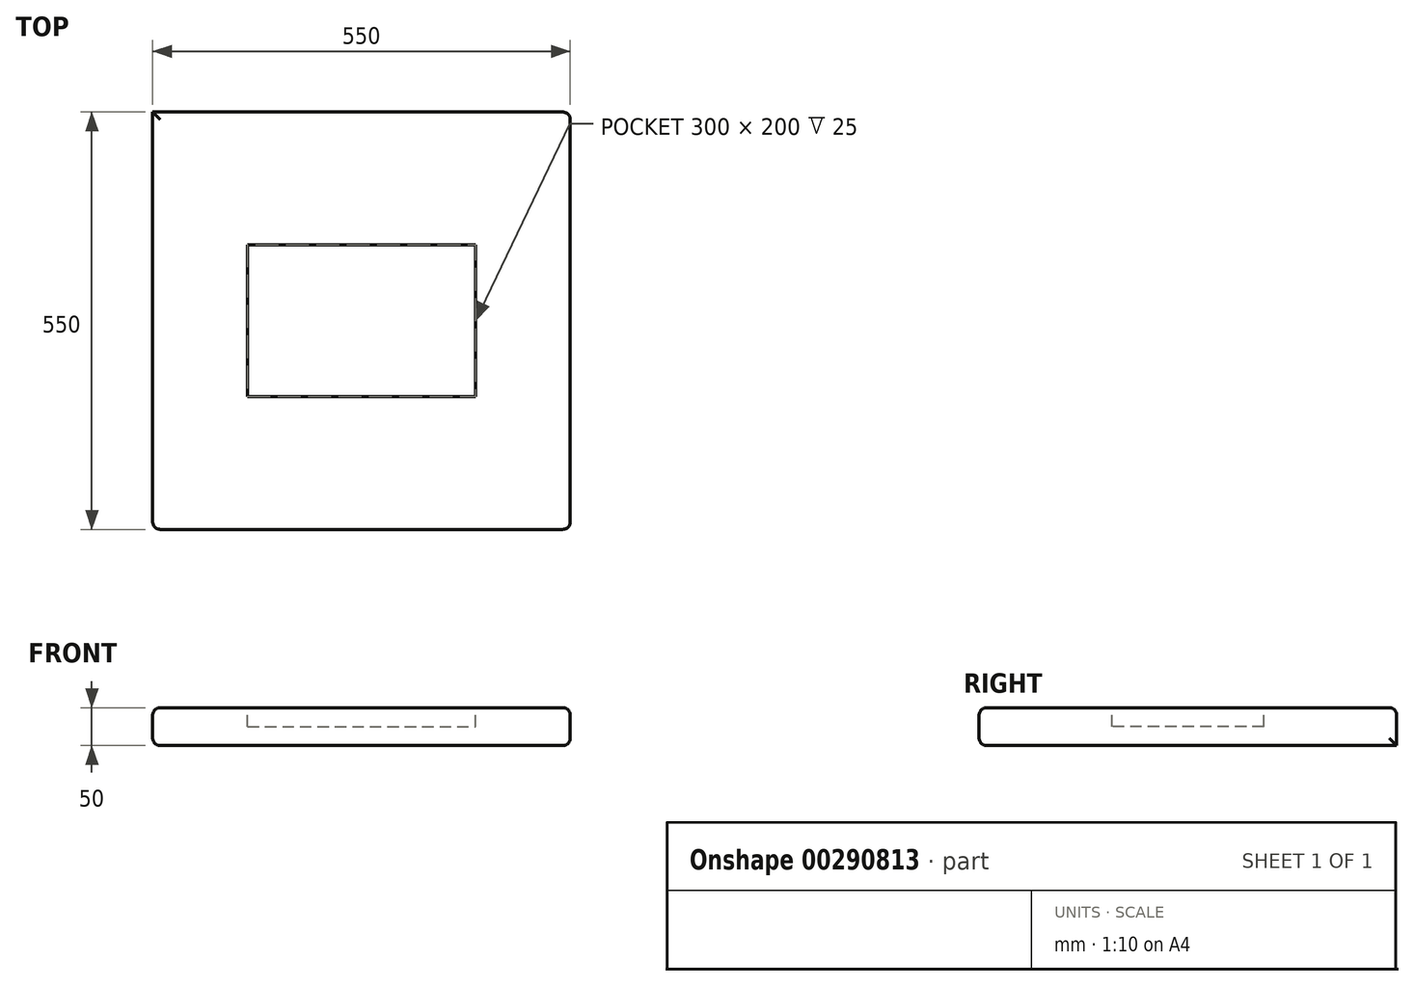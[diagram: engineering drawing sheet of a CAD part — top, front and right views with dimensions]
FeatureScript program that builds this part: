
annotation { "Feature Type Name" : "Feature", "Feature Type Description" : "" }
export const myFeature = defineFeature(function(context is Context, id is Id, definition is map)
    precondition{}
    {
        {
            var Q0;
            Q0=qCreatedBy(makeId("Top.planeOp"),FACE);
            var sketch = newSketch(context, id + "F0", { "sketchPlane" : qUnion([Q0])});
            skLineSegment(sketch, "E0.bottom", {"start": v(275, 275) * mm, "end": v(-275, 275) * mm});
            skLineSegment(sketch, "E0.top", {"start": v(275, -275) * mm, "end": v(-275, -275) * mm});
            skLineSegment(sketch, "E0.left", {"start": v(275, 275) * mm, "end": v(275, -275) * mm});
            skLineSegment(sketch, "E0.right", {"start": v(-275, 275) * mm, "end": v(-275, -275) * mm});
            skPoint(sketch, "E0.middle", {"position": v(0, 0) * mm});
            skSolve(sketch);
        }
        {
            var Q0;
            Q0=makeQuery(id+"F0.imprint","IMPRINT",FACE,{"disambiguationData":[TD([[makeQuery(id+"F0.imprint","IMPRINT",EDGE,{"derivedFrom":sQuery(id+"F0.wireOp",EDGE,"E0.bottom")}),1.0]])]});
            extrude(context, id + "F1", {"entities" : qUnion([Q0]), "depth" : 50 * mm});
        }
        {
            var Q0;
            Q0=makeQuery(id+"F1.opExtrude","CAP_EDGE",EDGE,{"disambiguationData":[OSD([sQuery(id+"F0.wireOp",EDGE,"E0.right")])],"isStart":false});
            var Q1;
            Q1=makeQuery(id+"F1.opExtrude","CAP_EDGE",EDGE,{"disambiguationData":[OSD([sQuery(id+"F0.wireOp",EDGE,"E0.top")])],"isStart":false});
            var Q2;
            Q2=makeQuery(id+"F1.opExtrude","CAP_EDGE",EDGE,{"disambiguationData":[OSD([sQuery(id+"F0.wireOp",EDGE,"E0.left")])],"isStart":true});
            var Q3;
            Q3=makeQuery(id+"F1.opExtrude","SWEPT_EDGE",EDGE,{"disambiguationData":[OSD([sQuery(id+"F0.wireOp",EDGE,"E0.top"),sQuery(id+"F0.wireOp",EDGE,"E0.left")])]});
            var Q4;
            Q4=makeQuery(id+"F1.opExtrude","SWEPT_EDGE",EDGE,{"disambiguationData":[OSD([sQuery(id+"F0.wireOp",EDGE,"E0.bottom"),sQuery(id+"F0.wireOp",EDGE,"E0.left")])]});
            var Q5;
            Q5=makeQuery(id+"F1.opExtrude","CAP_EDGE",EDGE,{"disambiguationData":[OSD([sQuery(id+"F0.wireOp",EDGE,"E0.left")])],"isStart":false});
            var Q6;
            Q6=makeQuery(id+"F1.opExtrude","CAP_EDGE",EDGE,{"disambiguationData":[OSD([sQuery(id+"F0.wireOp",EDGE,"E0.bottom")])],"isStart":false});
            var Q7;
            Q7=makeQuery(id+"F1.opExtrude","CAP_EDGE",EDGE,{"disambiguationData":[OSD([sQuery(id+"F0.wireOp",EDGE,"E0.top")])],"isStart":true});
            var Q8;
            Q8=makeQuery(id+"F1.opExtrude","SWEPT_EDGE",EDGE,{"disambiguationData":[OSD([sQuery(id+"F0.wireOp",EDGE,"E0.top"),sQuery(id+"F0.wireOp",EDGE,"E0.right")])]});
            var Q9;
            Q9=makeQuery(id+"F1.opExtrude","CAP_EDGE",EDGE,{"disambiguationData":[OSD([sQuery(id+"F0.wireOp",EDGE,"E0.right")])],"isStart":true});
            fillet(context, id + "F2", {"entities" : qUnion([Q0, Q1, Q2, Q3, Q4, Q5, Q6, Q7, Q8, Q9]), "radius" : 10 * mm, "tangentPropagation" : true, "allowEdgeOverflow" : false});
        }
        {
            var Q0;
            Q0=makeQuery(id+"F1.opExtrude","CAP_FACE",FACE,{"disambiguationData":[OSD([sQuery(id+"F0.wireOp",EDGE,"E0.bottom"),sQuery(id+"F0.wireOp",EDGE,"E0.top"),sQuery(id+"F0.wireOp",EDGE,"E0.left"),sQuery(id+"F0.wireOp",EDGE,"E0.right")])],"isStart":false});
            var sketch = newSketch(context, id + "F3", { "sketchPlane" : qUnion([Q0])});
            skLineSegment(sketch, "E1.bottom", {"start": v(-150, 100) * mm, "end": v(150, 100) * mm});
            skLineSegment(sketch, "E1.top", {"start": v(-150, -100) * mm, "end": v(150, -100) * mm});
            skLineSegment(sketch, "E1.left", {"start": v(-150, 100) * mm, "end": v(-150, -100) * mm});
            skLineSegment(sketch, "E1.right", {"start": v(150, 100) * mm, "end": v(150, -100) * mm});
            skPoint(sketch, "E1.middle", {"position": v(0, 0) * mm});
            skSolve(sketch);
        }
        {
            var Q0;
            Q0=makeQuery(id+"F3.imprint","IMPRINT",FACE,{"disambiguationData":[TD([[makeQuery(id+"F3.imprint","IMPRINT",EDGE,{"derivedFrom":sQuery(id+"F3.wireOp",EDGE,"E1.bottom")}),-1.0]])]});
            extrude(context, id + "F4", {"entities" : qUnion([Q0]), "operationType" : NewBodyOperationType.REMOVE, "oppositeDirection" : true, "depth" : 25 * mm});
        }
    });
